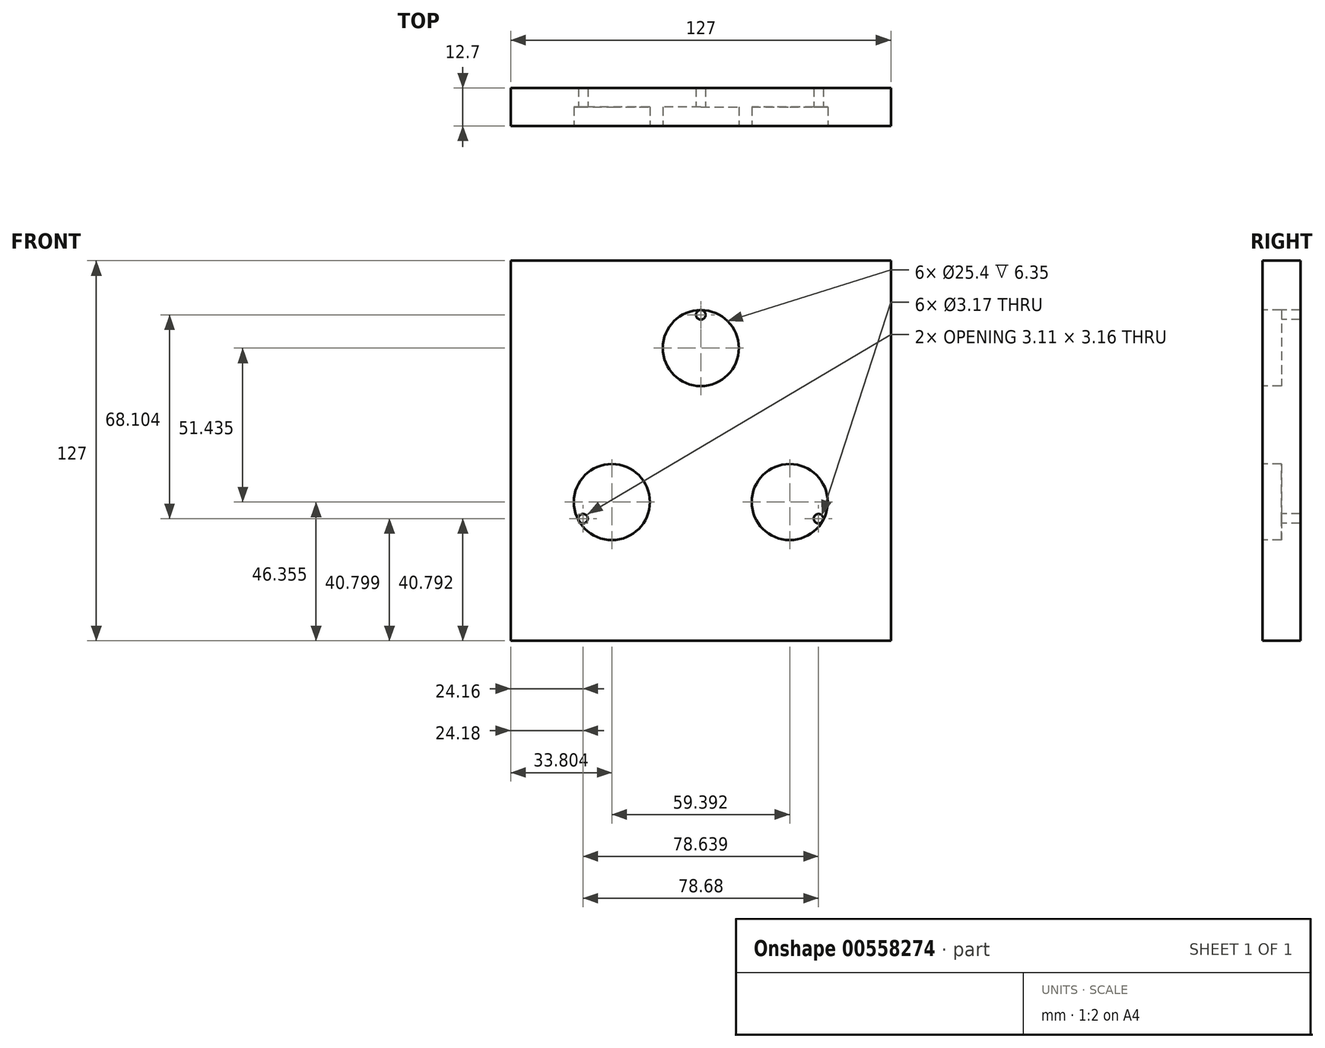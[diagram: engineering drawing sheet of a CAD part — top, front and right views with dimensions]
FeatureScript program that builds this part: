
annotation { "Feature Type Name" : "Feature", "Feature Type Description" : "" }
export const myFeature = defineFeature(function(context is Context, id is Id, definition is map)
    precondition{}
    {
        {
            var Q0;
            Q0=qCreatedBy(makeId("Front.planeOp"),FACE);
            var sketch = newSketch(context, id + "F0", { "sketchPlane" : qUnion([Q0])});
            skLineSegment(sketch, "E0.bottom", {"start": v(63.5, 63.5) * mm, "end": v(-63.5, 63.5) * mm});
            skLineSegment(sketch, "E0.top", {"start": v(63.5, -63.5) * mm, "end": v(-63.5, -63.5) * mm});
            skLineSegment(sketch, "E0.left", {"start": v(63.5, 63.5) * mm, "end": v(63.5, -63.5) * mm});
            skLineSegment(sketch, "E0.right", {"start": v(-63.5, 63.5) * mm, "end": v(-63.5, -63.5) * mm});
            skPoint(sketch, "E0.middle", {"position": v(0, 0) * mm});
            skSolve(sketch);
        }
        {
            var Q0;
            Q0 = qSketchRegion(id + "F0", true);
            extrude(context, id + "F1", {"entities" : qUnion([Q0]), "depth" : 12.7 * mm, "offsetDistance" : 25.4 * mm});
        }
        {
            var Q0;
            Q0=makeQuery(id+"F1.opExtrude","CAP_FACE",FACE,{"disambiguationData":[OSD([sQuery(id+"F0.wireOp",EDGE,"E0.bottom"),sQuery(id+"F0.wireOp",EDGE,"E0.top"),sQuery(id+"F0.wireOp",EDGE,"E0.left"),sQuery(id+"F0.wireOp",EDGE,"E0.right")])],"isStart":false});
            var sketch = newSketch(context, id + "F2", { "sketchPlane" : qUnion([Q0])});
            skCircle(sketch, "E1", {"center": v(0, 0) * mm, "radius": 34.3 * mm, "construction": true});
            skCircle(sketch, "E2", {"center": v(0, 34.3) * mm, "radius": 12.7 * mm});
            skCircle(sketch, "E3", {"center": v(0, 0) * mm, "radius": 21.59 * mm, "construction": true});
            skCircle(sketch, "E4.1.0", {"center": v(-29.7, -17.14) * mm, "radius": 12.7 * mm});
            skCircle(sketch, "E4.2.0", {"center": v(29.7, -17.15) * mm, "radius": 12.7 * mm});
            skSolve(sketch);
        }
        {
            var Q0;
            Q0 = qSketchRegion(id + "F2", true);
            extrude(context, id + "F3", {"entities" : qUnion([Q0]), "operationType" : NewBodyOperationType.REMOVE, "oppositeDirection" : true, "depth" : 6.35 * mm, "offsetDistance" : 25.4 * mm});
        }
        {
            var Q0;
            Q0=makeQuery(id+"F3.boolean.opBoolean","COPY",FACE,{"derivedFrom":makeQuery(id+"F3.opExtrude","CAP_FACE",FACE,{"disambiguationData":[OSD([sQuery(id+"F2.wireOp",EDGE,"E2")])],"isStart":false})});
            var sketch = newSketch(context, id + "F4", { "sketchPlane" : qUnion([Q0])});
            skCircle(sketch, "E5", {"center": v(0, 0) * mm, "radius": 45.4 * mm, "construction": true});
            skCircle(sketch, "E6", {"center": v(0, 45.4) * mm, "radius": 1.59 * mm});
            skCircle(sketch, "E7.1.0", {"center": v(-39.32, -22.7) * mm, "radius": 1.59 * mm});
            skCircle(sketch, "E7.2.0", {"center": v(39.32, -22.7) * mm, "radius": 1.59 * mm});
            skSolve(sketch);
        }
        {
            var Q0;
            Q0 = qSketchRegion(id + "F4", true);
            extrude(context, id + "F5", {"entities" : qUnion([Q0]), "operationType" : NewBodyOperationType.REMOVE, "endBound" : BoundingType.THROUGH_ALL, "oppositeDirection" : true, "depth" : 25.4 * mm, "offsetDistance" : 25.4 * mm});
        }
    });
